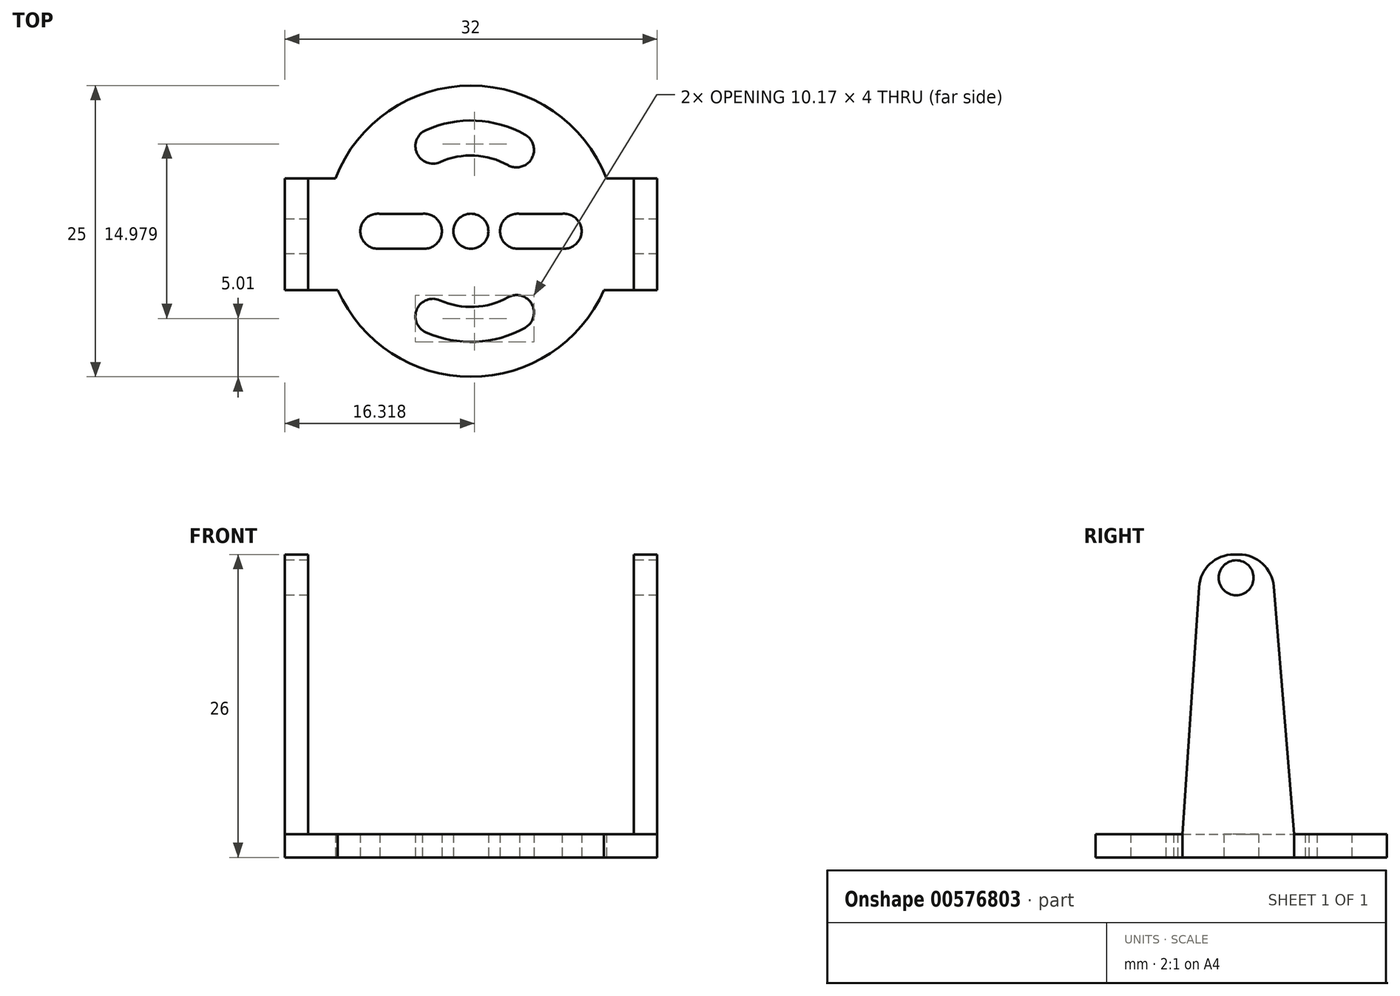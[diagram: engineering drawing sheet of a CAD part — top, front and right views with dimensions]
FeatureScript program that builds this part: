
annotation { "Feature Type Name" : "Feature", "Feature Type Description" : "" }
export const myFeature = defineFeature(function(context is Context, id is Id, definition is map)
    precondition{}
    {
        {
            var Q0;
            Q0=qCreatedBy(makeId("Top.planeOp"),FACE);
            var sketch = newSketch(context, id + "F0", { "sketchPlane" : qUnion([Q0])});
            skCircle(sketch, "E0", {"center": v(0, 0) * mm, "radius": 12.5 * mm});
            skSolve(sketch);
        }
        {
            var Q0;
            Q0=qCreatedBy(makeId("Top.planeOp"),FACE);
            var sketch = newSketch(context, id + "F1", { "sketchPlane" : qUnion([Q0])});
            skLineSegment(sketch, "E1", {"start": v(-16, 0) * mm, "end": v(-16, 4.54) * mm});
            skLineSegment(sketch, "E2", {"start": v(-16, 4.54) * mm, "end": v(16, 4.54) * mm});
            skLineSegment(sketch, "E3", {"start": v(16, 4.54) * mm, "end": v(16, -5.06) * mm});
            skLineSegment(sketch, "E4", {"start": v(16, -5.06) * mm, "end": v(-16, -5.06) * mm});
            skLineSegment(sketch, "E5", {"start": v(-16, -5.06) * mm, "end": v(-16, 0) * mm});
            skSolve(sketch);
        }
        {
            var Q0;
            Q0 = qSketchRegion(id + "F0", true);
            extrude(context, id + "F2", {"entities" : qUnion([Q0]), "depth" : 2 * mm, "offsetDistance" : 25 * mm});
        }
        {
            var Q0;
            Q0 = qSketchRegion(id + "F1", true);
            extrude(context, id + "F3", {"entities" : qUnion([Q0]), "operationType" : NewBodyOperationType.ADD, "depth" : 2 * mm, "offsetDistance" : 25 * mm});
        }
        {
            var Q0;
            Q0=makeQuery(id+"F3.opExtrude","SWEPT_FACE",FACE,{"disambiguationData":[OSD([sQuery(id+"F1.wireOp",EDGE,"E3")])]});
            var sketch = newSketch(context, id + "F4", { "sketchPlane" : qUnion([Q0])});
            skLineSegment(sketch, "E6", {"start": v(-5.06, 2) * mm, "end": v(-3.45, 26) * mm});
            skLineSegment(sketch, "E7", {"start": v(-3.45, 26) * mm, "end": v(2.55, 26) * mm});
            skLineSegment(sketch, "E8", {"start": v(2.55, 26) * mm, "end": v(4.54, 2) * mm});
            skLineSegment(sketch, "E9", {"start": v(4.54, 2) * mm, "end": v(-5.06, 2) * mm});
            skSolve(sketch);
        }
        {
            var Q0;
            Q0=makeQuery(id+"F3.opExtrude","SWEPT_FACE",FACE,{"disambiguationData":[OSD([sQuery(id+"F1.wireOp",EDGE,"E1"),sQuery(id+"F1.wireOp",EDGE,"E5")])]});
            var sketch = newSketch(context, id + "F5", { "sketchPlane" : qUnion([Q0])});
            skPoint(sketch, "E10.0", {"position": v(-2.55, 26) * mm});
            skPoint(sketch, "E11.0", {"position": v(3.45, 26) * mm});
            skLineSegment(sketch, "E12", {"start": v(-4.54, 2) * mm, "end": v(-2.55, 26) * mm});
            skLineSegment(sketch, "E13", {"start": v(3.45, 26) * mm, "end": v(5.06, 2) * mm});
            skLineSegment(sketch, "E14", {"start": v(5.06, 2) * mm, "end": v(-4.54, 2) * mm});
            skLineSegment(sketch, "E15", {"start": v(-2.55, 26) * mm, "end": v(3.45, 26) * mm});
            skSolve(sketch);
        }
        {
            var Q0;
            Q0 = qSketchRegion(id + "F4", true);
            extrude(context, id + "F6", {"entities" : qUnion([Q0]), "operationType" : NewBodyOperationType.ADD, "oppositeDirection" : true, "depth" : 2 * mm, "offsetDistance" : 25 * mm});
        }
        {
            var Q0;
            Q0 = qSketchRegion(id + "F5", true);
            extrude(context, id + "F7", {"entities" : qUnion([Q0]), "operationType" : NewBodyOperationType.ADD, "oppositeDirection" : true, "depth" : 2 * mm, "offsetDistance" : 25 * mm});
        }
        {
            var Q0;
            Q0=makeQuery(id+"F7.boolean.opBoolean","MERGE",FACE,{"derivedFrom":[makeQuery(id+"F3.opExtrude","SWEPT_FACE",FACE,{"disambiguationData":[OSD([sQuery(id+"F1.wireOp",EDGE,"E1"),sQuery(id+"F1.wireOp",EDGE,"E5")])]}),makeQuery(id+"F7.opExtrude","CAP_FACE",FACE,{"disambiguationData":[OSD([sQuery(id+"F5.wireOp",EDGE,"E12"),sQuery(id+"F5.wireOp",EDGE,"E13"),sQuery(id+"F5.wireOp",EDGE,"E14"),sQuery(id+"F5.wireOp",EDGE,"E15")])],"isStart":true})]});
            var sketch = newSketch(context, id + "F8", { "sketchPlane" : qUnion([Q0])});
            skCircle(sketch, "E16", {"center": v(0.45, 24) * mm, "radius": 1.5 * mm});
            skPoint(sketch, "E16.centerSnap0", {"position": v(0.45, 26) * mm});
            skSolve(sketch);
        }
        {
            var Q0;
            Q0=makeQuery(id+"F7.opExtrude","SWEPT_EDGE",EDGE,{"disambiguationData":[OSD([sQuery(id+"F5.wireOp",EDGE,"E12"),sQuery(id+"F5.wireOp",EDGE,"E15")])]});
            var Q1;
            Q1=makeQuery(id+"F7.opExtrude","SWEPT_EDGE",EDGE,{"disambiguationData":[OSD([sQuery(id+"F5.wireOp",EDGE,"E13"),sQuery(id+"F5.wireOp",EDGE,"E15")])]});
            var Q2;
            Q2=makeQuery(id+"F6.opExtrude","SWEPT_EDGE",EDGE,{"disambiguationData":[OSD([sQuery(id+"F4.wireOp",EDGE,"E7"),sQuery(id+"F4.wireOp",EDGE,"E8")])]});
            var Q3;
            Q3=makeQuery(id+"F6.opExtrude","SWEPT_EDGE",EDGE,{"disambiguationData":[OSD([sQuery(id+"F4.wireOp",EDGE,"E6"),sQuery(id+"F4.wireOp",EDGE,"E7")])]});
            fillet(context, id + "F9", {"entities" : qUnion([Q0, Q1, Q2, Q3]), "radius" : 3 * mm, "tangentPropagation" : true, "allowEdgeOverflow" : false});
        }
        {
            var Q0;
            Q0 = qSketchRegion(id + "F8", true);
            extrude(context, id + "F10", {"entities" : qUnion([Q0]), "operationType" : NewBodyOperationType.REMOVE, "oppositeDirection" : true, "depth" : 50 * mm, "offsetDistance" : 25 * mm});
        }
        {
            var Q0;
            Q0=makeQuery(id+"F3.boolean.opBoolean","MERGE",FACE,{"derivedFrom":[makeQuery(id+"F2.opExtrude","CAP_FACE",FACE,{"disambiguationData":[OSD([sQuery(id+"F0.wireOp",EDGE,"E0")])],"isStart":true}),makeQuery(id+"F3.opExtrude","CAP_FACE",FACE,{"disambiguationData":[OSD([sQuery(id+"F1.wireOp",EDGE,"E1"),sQuery(id+"F1.wireOp",EDGE,"E2"),sQuery(id+"F1.wireOp",EDGE,"E3"),sQuery(id+"F1.wireOp",EDGE,"E4"),sQuery(id+"F1.wireOp",EDGE,"E5")])],"isStart":true})]});
            var sketch = newSketch(context, id + "F11", { "sketchPlane" : qUnion([Q0])});
            skPoint(sketch, "E17.startSnap0", {"position": v(-13.71, 5.06) * mm});
            skPoint(sketch, "E18.middle", {"position": v(-10.5, 0) * mm});
            skPoint(sketch, "E19.1.0.0", {"position": v(10.5, 0) * mm});
            skCircle(sketch, "E20", {"center": v(0, 0) * mm, "radius": 1.5 * mm});
            skSolve(sketch);
        }
        {
            var Q0;
            Q0=makeQuery(id+"F11.imprint","IMPRINT",FACE,{"disambiguationData":[TD([[makeQuery(id+"F11.imprint","IMPRINT",EDGE,{"derivedFrom":sQuery(id+"F11.wireOp",EDGE,"E20")}),-1.0]])]});
            var sketch = newSketch(context, id + "F12", { "sketchPlane" : qUnion([Q0])});
            skArc(sketch, "E21", {"start": v(-3.27, 7.3) * mm, "mid": v(0.36, 8) * mm, "end": v(3.91, 6.98) * mm});
            skArc(sketch, "E22.0.startCap", {"start": v(-2.65, 5.93) * mm, "mid": v(-4.63, 6.7) * mm, "end": v(-3.88, 8.67) * mm});
            skArc(sketch, "E22.0.endCap", {"start": v(4.65, 8.29) * mm, "mid": v(5.22, 6.25) * mm, "end": v(3.18, 5.67) * mm});
            skArc(sketch, "E22.0.left", {"start": v(-3.88, 8.67) * mm, "mid": v(0.43, 9.5) * mm, "end": v(4.65, 8.29) * mm});
            skArc(sketch, "E22.0.right", {"start": v(-2.65, 5.93) * mm, "mid": v(0.3, 6.5) * mm, "end": v(3.18, 5.67) * mm});
            skArc(sketch, "E23.MirrorCS", {"start": v(-3.27, -7.3) * mm, "mid": v(0.36, -8) * mm, "end": v(3.91, -6.98) * mm});
            skArc(sketch, "E24.MirrorCS", {"start": v(-3.88, -8.67) * mm, "mid": v(0.43, -9.5) * mm, "end": v(4.65, -8.29) * mm});
            skArc(sketch, "E25.MirrorCS", {"start": v(4.65, -8.29) * mm, "mid": v(5.22, -6.25) * mm, "end": v(3.18, -5.67) * mm});
            skArc(sketch, "E26.MirrorCS", {"start": v(-2.65, -5.93) * mm, "mid": v(-4.63, -6.7) * mm, "end": v(-3.88, -8.67) * mm});
            skArc(sketch, "E27.MirrorCS", {"start": v(-2.65, -5.93) * mm, "mid": v(0.3, -6.5) * mm, "end": v(3.18, -5.67) * mm});
            skSolve(sketch);
        }
        {
            var Q0;
            Q0 = qSketchRegion(id + "F12", true);
            extrude(context, id + "F13", {"entities" : qUnion([Q0]), "operationType" : NewBodyOperationType.REMOVE, "oppositeDirection" : true, "depth" : 25 * mm, "offsetDistance" : 25 * mm});
        }
        {
            var Q0;
            Q0=makeQuery(id+"F11.imprint","IMPRINT",FACE,{"disambiguationData":[TD([[makeQuery(id+"F11.imprint","IMPRINT",EDGE,{"derivedFrom":sQuery(id+"F11.wireOp",EDGE,"E20")}),-1.0]])]});
            var sketch = newSketch(context, id + "F14", { "sketchPlane" : qUnion([Q0])});
            skCircle(sketch, "E28", {"center": v(-4, 0) * mm, "radius": 1.5 * mm});
            skCircle(sketch, "E29", {"center": v(-8, 0) * mm, "radius": 1.5 * mm});
            skLineSegment(sketch, "E30", {"start": v(-8.17, 1.49) * mm, "end": v(-4.17, 1.49) * mm});
            skLineSegment(sketch, "E31", {"start": v(-4.17, 1.49) * mm, "end": v(-4.17, -1.49) * mm});
            skLineSegment(sketch, "E32", {"start": v(-4.17, -1.49) * mm, "end": v(-8.17, -1.49) * mm});
            skLineSegment(sketch, "E33", {"start": v(-8.17, -1.49) * mm, "end": v(-8.17, 1.49) * mm});
            skLineSegment(sketch, "E34.1.0.0", {"start": v(3.83, 1.49) * mm, "end": v(7.83, 1.49) * mm});
            skCircle(sketch, "E34.1.0.1", {"center": v(4, 0) * mm, "radius": 1.5 * mm});
            skLineSegment(sketch, "E34.1.0.2", {"start": v(7.83, -1.49) * mm, "end": v(3.83, -1.49) * mm});
            skCircle(sketch, "E34.1.0.3", {"center": v(8, 0) * mm, "radius": 1.5 * mm});
            skLineSegment(sketch, "E34.1.0.4", {"start": v(3.83, -1.49) * mm, "end": v(3.83, 1.49) * mm});
            skLineSegment(sketch, "E34.1.0.5", {"start": v(7.83, 1.49) * mm, "end": v(7.83, -1.49) * mm});
            skLineSegment(sketch, "E34.direction1", {"start": v(-8.17, -1.49) * mm, "end": v(3.83, -1.49) * mm, "construction": true});
            skCircle(sketch, "E35", {"center": v(0, 0) * mm, "radius": 1.5 * mm});
            skSolve(sketch);
        }
        {
            var Q0;
            Q0 = qSketchRegion(id + "F14", true);
            extrude(context, id + "F15", {"entities" : qUnion([Q0]), "operationType" : NewBodyOperationType.REMOVE, "oppositeDirection" : true, "depth" : 4 * mm, "offsetDistance" : 25 * mm});
        }
    });
